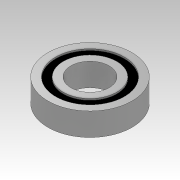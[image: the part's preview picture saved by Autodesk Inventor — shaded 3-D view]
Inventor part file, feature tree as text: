
AUTODESK INVENTOR PART (.ipt)
format: ipt  version: 2020 (Build 240168000, 168)  size: 128,000 bytes
history: native  units: mm
features: revolve x1, sketch x1
ambient origin geometry x8: Origin, YZ Plane, XZ Plane, XY Plane, X Axis, Y Axis, Z Axis, Center Point
bodies: Solid1 (feature_tree)
feature tree (2):
  revolve  "Revolution1"  [1 undecoded]
  sketch  "Sketch1"  dims[d0=2.5mm d2=3.0mm d5=5.5mm d6=0.2mm d7=1.0mm d8=90.0deg]
note: 1 required parameter value undecoded (feature->parameter linkage not recoverable at this tier; creation-order binding heuristic only, values carry confidence <= 0.55)
